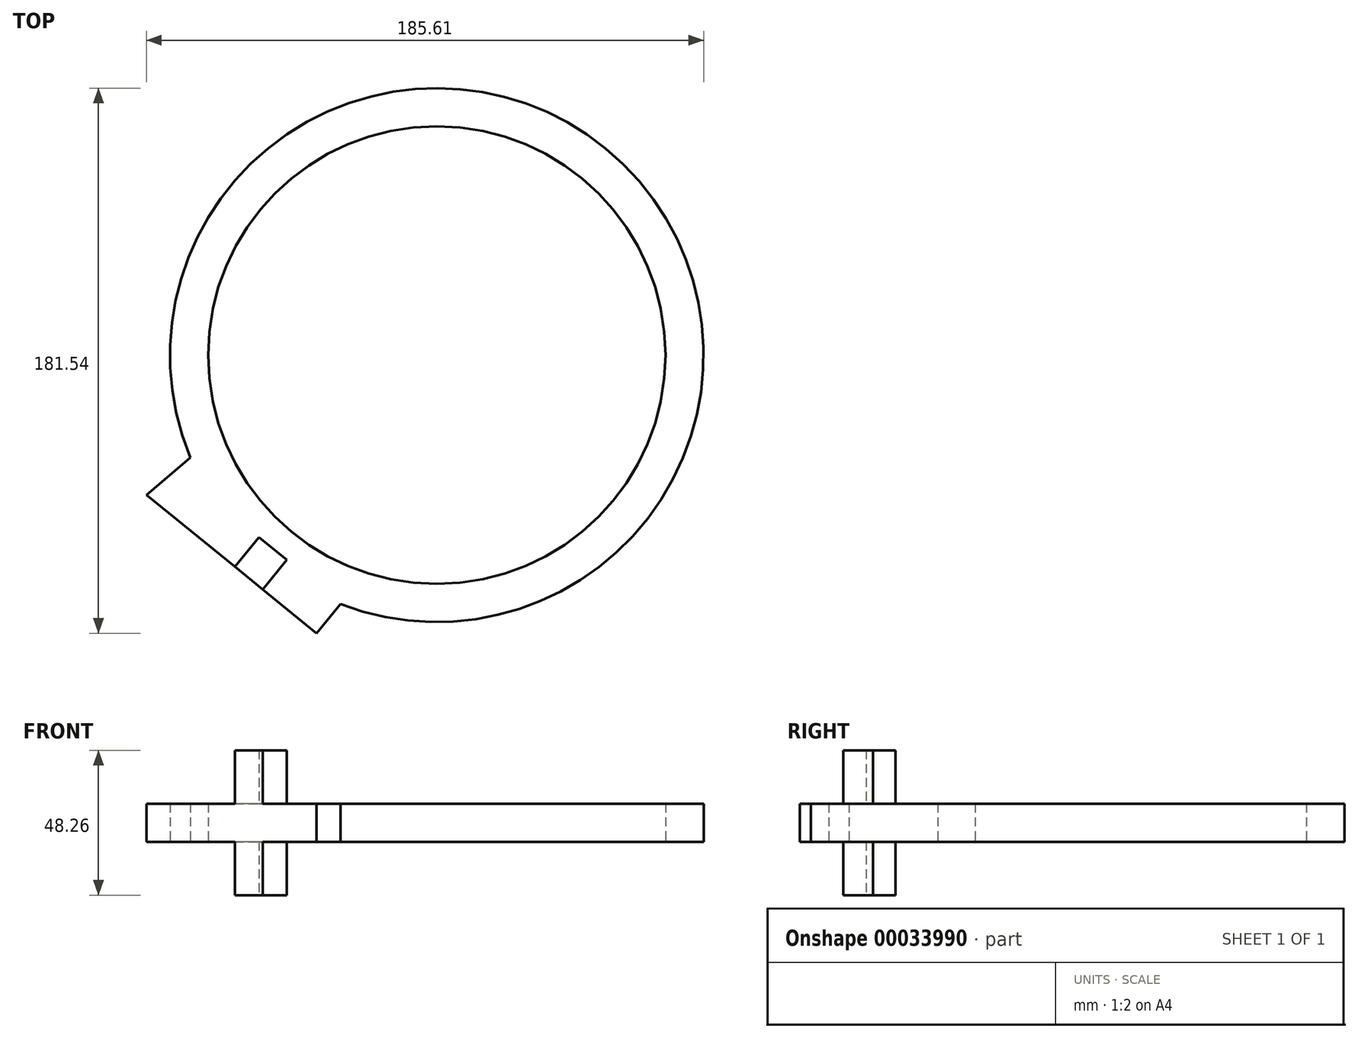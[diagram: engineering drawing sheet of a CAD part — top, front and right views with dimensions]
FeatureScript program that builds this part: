
annotation { "Feature Type Name" : "Feature", "Feature Type Description" : "" }
export const myFeature = defineFeature(function(context is Context, id is Id, definition is map)
    precondition{}
    {
        {
            var Q0;
            Q0=qCreatedBy(makeId("Top.planeOp"),FACE);
            var sketch = newSketch(context, id + "F0", { "sketchPlane" : qUnion([Q0])});
            skCircle(sketch, "E0", {"center": v(0, 0) * mm, "radius": 88.9 * mm});
            skCircle(sketch, "E1", {"center": v(0, 0) * mm, "radius": 76.2 * mm});
            skSolve(sketch);
        }
        {
            var Q0;
            Q0 = qSketchRegion(id + "F0", true);
            extrude(context, id + "F1", {"entities" : qUnion([Q0]), "depth" : 12.7 * mm});
        }
        {
            var Q0;
            Q0=makeQuery(id+"F1.opExtrude","CAP_FACE",FACE,{"disambiguationData":[OSD([sQuery(id+"F0.wireOp",EDGE,"E0"),sQuery(id+"F0.wireOp",EDGE,"E1")])],"isStart":true});
            var sketch = newSketch(context, id + "F2", { "sketchPlane" : qUnion([Q0])});
            skLineSegment(sketch, "E2", {"start": v(-82.06, 34.2) * mm, "end": v(-96.71, 46.58) * mm});
            skLineSegment(sketch, "E3", {"start": v(-96.71, 46.58) * mm, "end": v(-40.03, 92.64) * mm});
            skLineSegment(sketch, "E4", {"start": v(-40.03, 92.64) * mm, "end": v(-32.12, 82.9) * mm});
            skArc(sketch, "E5", {"start": v(-32.12, 82.9) * mm, "mid": v(-59.73, 61.26) * mm, "end": v(-82.06, 34.2) * mm});
            skSolve(sketch);
        }
        {
            var Q0;
            Q0 = qSketchRegion(id + "F2", true);
            extrude(context, id + "F3", {"entities" : qUnion([Q0]), "operationType" : NewBodyOperationType.ADD, "oppositeDirection" : true, "depth" : 12.7 * mm});
        }
        {
            var Q0;
            Q0=makeQuery(id+"F3.opExtrude","SWEPT_FACE",FACE,{"disambiguationData":[OSD([sQuery(id+"F2.wireOp",EDGE,"E3")])]});
            var sketch = newSketch(context, id + "F4", { "sketchPlane" : qUnion([Q0])});
            skLineSegment(sketch, "E6.bottom", {"start": v(4.28, 30.48) * mm, "end": v(-7.73, 30.48) * mm});
            skLineSegment(sketch, "E6.top", {"start": v(4.28, -17.78) * mm, "end": v(-7.73, -17.78) * mm});
            skLineSegment(sketch, "E6.left", {"start": v(4.28, 30.48) * mm, "end": v(4.28, -17.78) * mm});
            skLineSegment(sketch, "E6.right", {"start": v(-7.73, 30.48) * mm, "end": v(-7.73, -17.78) * mm});
            skSolve(sketch);
        }
        {
            var Q0;
            Q0 = qSketchRegion(id + "F4", true);
            extrude(context, id + "F5", {"entities" : qUnion([Q0]), "operationType" : NewBodyOperationType.ADD, "oppositeDirection" : true, "depth" : 12.7 * mm});
        }
    });
